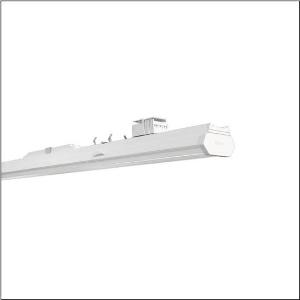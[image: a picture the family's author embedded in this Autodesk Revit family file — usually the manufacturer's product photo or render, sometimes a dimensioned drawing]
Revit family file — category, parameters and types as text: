
# Revit family: licross_21_protected_mo_52td1b7n48xg
name_source: partatom
category: Lighting Fixtures
units: mm (PartAtom-declared; Revit-internal decimal feet)

## family parameters
Cut with Voids When Loaded = No
Host = Face
Light Source = No
Part Type = Normal
Room Calculation Point = No
Round Connector Dimension = Use Diameter
Shared = No

## types (1)
- Licross 21 Protected MO (1 x LED, 8090 lm, 47.9 W, 4000K)
    Apparent Load = 48 VA
    CIE Flux Codes = 54 82 95 97 100
    Color Rendering = 80
    Color Temperature = 4000K
    Default Elevation = 1800 mm
    Description = Licross 21 Protected MO, luminaire insert, of sheet steel, galvanised, coil coated, white, length: 1.500mm, width: 90mm, height: 103mm, LED rated luminous flux: 8.090lm, light colour: 840, SDCM (Standard Deviation of Colour Matching)MacAdam ≤ 3 SDCM (initial), control gear: ON/OFF, with plug, 3-pole, with phase selection, mains connection: 220..240V, AC, 50/60Hz, rated input power: 48W, internal wiring halogen-free, primary optical cover: cover, of PMMA, light emission: direct distribution, primary light characteristic: symmetric, protection rating (complete): IP54, insulation class (complete): insulation class I (protective earthing), certification: CE, ENEC, VDE, UKCA, protection symbol: D if used in an environment with non-conductive dust loads with corresponding accessories, impact resistance: IK06, permissible ambient temperature for indoor applications: -35..+45°C, corresponds to IFS (International Featured Standards) requirements for safety and quality in the food industry, reducing of maximum allowable ambient temperature of 5°C with ceiling mounting, LABS conformity tested according to VDMA 24364:2018-05, The light source and the operating device comply with the requirements of the Ecodesign Regulation (EU) 2019/2020 and are replaceable in accordance with this regulation, packaging unit: 1 piece
    Height = 92 mm
    Lamp = 1 x LED
    Lamp Light Flux = 8090 lm
    Lamp Power = 47.9 W
    Lamp count = 1
    Length = 1500 mm
    Luminous efficacy = 169 lm/W
    Manufacturer = Siteco
    ModVariant = No
    Model = 52TD1B7N48XG
    Mounting Place = Ceiling
    Mounting Type = Pendant
    Number of Poles = 1
    OnlyDefault = Yes
    Power Factor = 1
    Product Name = Licross 21 Protected MO
    Product group = luminaire insert | ceiling pendant
    ProductGroupID = 901
    Protection Class = Protection class I
    Protection Degree = IP 54
    RLX_Detail_Level = 1
    RLX_Emergency_Light_Flux = 0 lm
    RLX_Emergency_Type = 0
    RLX_Emergency_Type_DB = No
    RlxData = <blob elided: 20993 chars, md5=9e92a4b6>
    Socket = socket
    Standby Power = 0 W
    System Light Flux = 8090 lm
    System Power = 48 W
    Type Comments = Product without accessories
    Type Image = l_1256148.jpg
    URL = http://relux.com
    VarID = ---
    Voltage = 0 V
    Weight = 0.00 kg
    Width = 88 mm

## geometry (parser evidence)
native form markers: Blend x4, Sweep x9
no freeform markers — native parametric forms only
